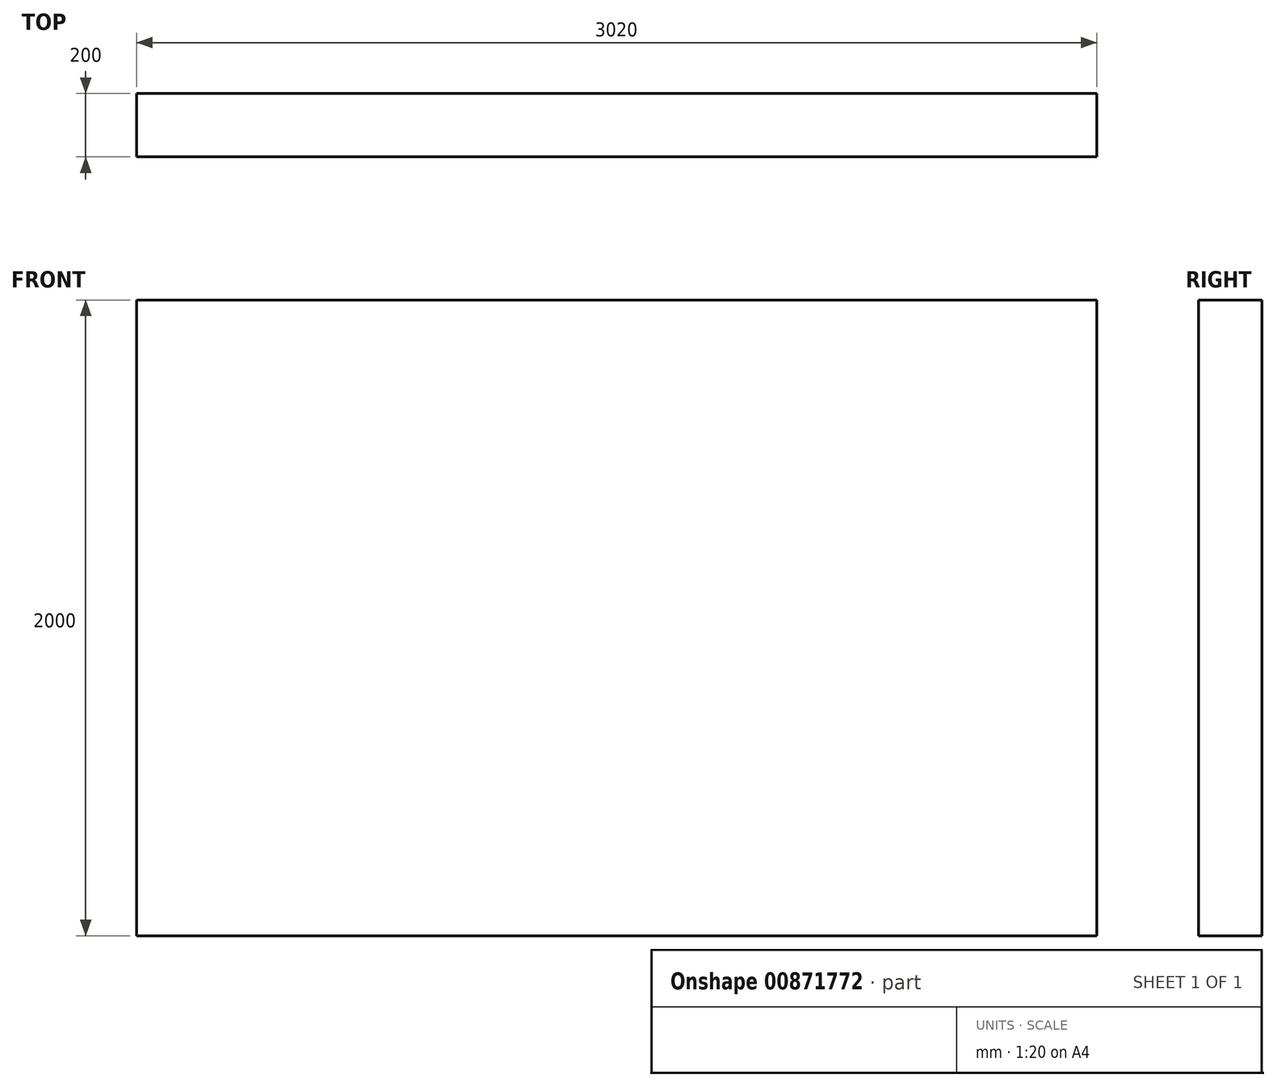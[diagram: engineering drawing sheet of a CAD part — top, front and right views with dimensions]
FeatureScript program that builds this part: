
annotation { "Feature Type Name" : "Feature", "Feature Type Description" : "" }
export const myFeature = defineFeature(function(context is Context, id is Id, definition is map)
    precondition{}
    {
        {
            var Q0;
            Q0=qCreatedBy(makeId("Front.planeOp"),FACE);
            var sketch = newSketch(context, id + "F0", { "sketchPlane" : qUnion([Q0])});
            skLineSegment(sketch, "E0.bottom", {"start": v(1510, 1000) * mm, "end": v(-1510, 1000) * mm});
            skLineSegment(sketch, "E0.top", {"start": v(1510, -1000) * mm, "end": v(-1510, -1000) * mm});
            skLineSegment(sketch, "E0.left", {"start": v(1510, 1000) * mm, "end": v(1510, -1000) * mm});
            skLineSegment(sketch, "E0.right", {"start": v(-1510, 1000) * mm, "end": v(-1510, -1000) * mm});
            skPoint(sketch, "E0.middle", {"position": v(0, 0) * mm});
            skSolve(sketch);
        }
        {
            var Q0;
            Q0=makeQuery(id+"F0.imprint","IMPRINT",FACE,{"disambiguationData":[TD([[makeQuery(id+"F0.imprint","IMPRINT",EDGE,{"derivedFrom":sQuery(id+"F0.wireOp",EDGE,"E0.bottom")}),1.0]])]});
            extrude(context, id + "F1", {"entities" : qUnion([Q0]), "oppositeDirection" : true, "depth" : 200 * mm, "offsetDistance" : 25 * mm});
        }
    });
